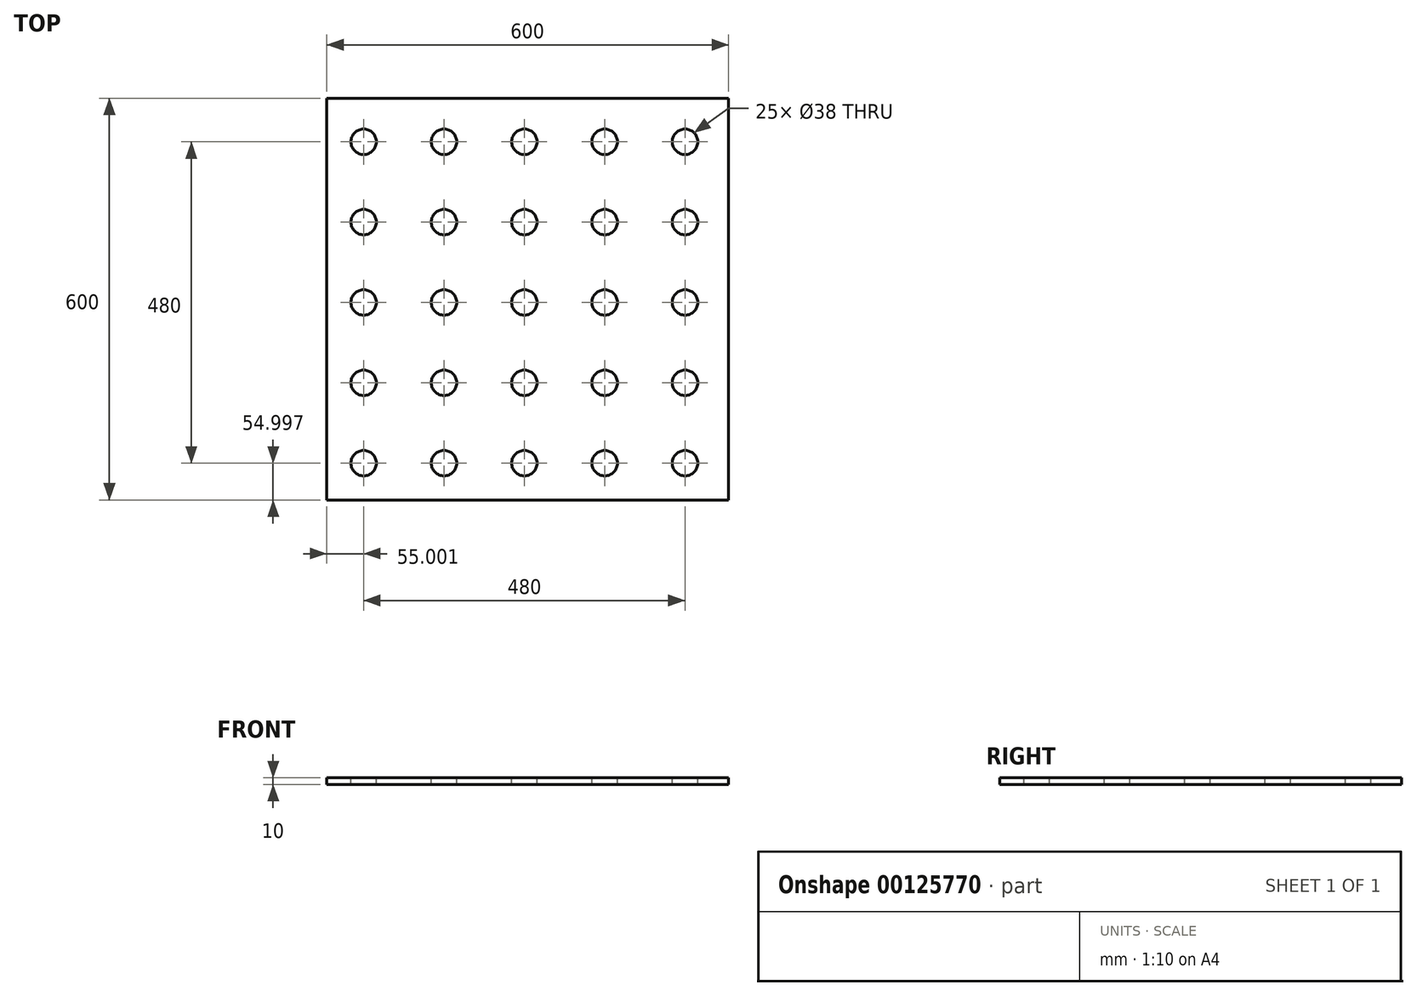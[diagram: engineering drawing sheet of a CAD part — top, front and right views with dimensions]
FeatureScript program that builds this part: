
annotation { "Feature Type Name" : "Feature", "Feature Type Description" : "" }
export const myFeature = defineFeature(function(context is Context, id is Id, definition is map)
    precondition{}
    {
        {
            var Q0;
            Q0=qCreatedBy(makeId("Top.planeOp"),FACE);
            var sketch = newSketch(context, id + "F0", { "sketchPlane" : qUnion([Q0])});
            skLineSegment(sketch, "E0.bottom", {"start": v(-275.03, 420.39) * mm, "end": v(324.97, 420.39) * mm});
            skLineSegment(sketch, "E0.top", {"start": v(-275.03, -179.61) * mm, "end": v(324.97, -179.61) * mm});
            skLineSegment(sketch, "E0.left", {"start": v(-275.03, 420.39) * mm, "end": v(-275.03, -179.61) * mm});
            skLineSegment(sketch, "E0.right", {"start": v(324.97, 420.39) * mm, "end": v(324.97, -179.61) * mm});
            skCircle(sketch, "E1", {"center": v(-220.03, -124.61) * mm, "radius": 19 * mm});
            skCircle(sketch, "E2.0.1.0", {"center": v(-220.03, -4.61) * mm, "radius": 19 * mm});
            skCircle(sketch, "E2.0.2.0", {"center": v(-220.03, 115.39) * mm, "radius": 19 * mm});
            skCircle(sketch, "E2.1.0.0", {"center": v(-100.03, -124.61) * mm, "radius": 19 * mm});
            skCircle(sketch, "E2.1.1.0", {"center": v(-100.03, -4.61) * mm, "radius": 19 * mm});
            skCircle(sketch, "E2.1.2.0", {"center": v(-100.03, 115.39) * mm, "radius": 19 * mm});
            skCircle(sketch, "E2.2.0.0", {"center": v(19.97, -124.61) * mm, "radius": 19 * mm});
            skCircle(sketch, "E2.2.1.0", {"center": v(19.97, -4.61) * mm, "radius": 19 * mm});
            skCircle(sketch, "E2.2.2.0", {"center": v(19.97, 115.39) * mm, "radius": 19 * mm});
            skLineSegment(sketch, "E2.direction1", {"start": v(-220.03, -124.61) * mm, "end": v(-100.03, -124.61) * mm, "construction": true});
            skLineSegment(sketch, "E2.direction2", {"start": v(-220.03, -124.61) * mm, "end": v(-220.03, -4.61) * mm, "construction": true});
            skCircle(sketch, "E3.0.3.0", {"center": v(139.97, -124.61) * mm, "radius": 19 * mm});
            skCircle(sketch, "E3.0.3.1", {"center": v(139.97, -4.61) * mm, "radius": 19 * mm});
            skCircle(sketch, "E3.0.3.2", {"center": v(139.97, 115.39) * mm, "radius": 19 * mm});
            skCircle(sketch, "E3.0.4.0", {"center": v(259.97, -124.61) * mm, "radius": 19 * mm});
            skCircle(sketch, "E3.0.4.1", {"center": v(259.97, -4.61) * mm, "radius": 19 * mm});
            skCircle(sketch, "E3.0.4.2", {"center": v(259.97, 115.39) * mm, "radius": 19 * mm});
            skCircle(sketch, "E4.0.0.3", {"center": v(-220.03, 235.39) * mm, "radius": 19 * mm});
            skCircle(sketch, "E4.0.1.3", {"center": v(-100.03, 235.39) * mm, "radius": 19 * mm});
            skCircle(sketch, "E4.0.2.3", {"center": v(19.97, 235.39) * mm, "radius": 19 * mm});
            skCircle(sketch, "E4.0.3.3", {"center": v(139.97, 235.39) * mm, "radius": 19 * mm});
            skCircle(sketch, "E4.0.4.3", {"center": v(259.97, 235.39) * mm, "radius": 19 * mm});
            skCircle(sketch, "E5.0.0.4", {"center": v(-220.03, 355.39) * mm, "radius": 19 * mm});
            skCircle(sketch, "E5.0.1.4", {"center": v(-100.03, 355.39) * mm, "radius": 19 * mm});
            skCircle(sketch, "E5.0.2.4", {"center": v(19.97, 355.39) * mm, "radius": 19 * mm});
            skCircle(sketch, "E5.0.3.4", {"center": v(139.97, 355.39) * mm, "radius": 19 * mm});
            skCircle(sketch, "E5.0.4.4", {"center": v(259.97, 355.39) * mm, "radius": 19 * mm});
            skSolve(sketch);
        }
        {
            var Q0;
            Q0=makeQuery(id+"F0.imprint","IMPRINT",FACE,{"disambiguationData":[TD([[makeQuery(id+"F0.imprint","IMPRINT",EDGE,{"derivedFrom":sQuery(id+"F0.wireOp",EDGE,"E0.bottom")}),-1.0]])]});
            extrude(context, id + "F1", {"entities" : qUnion([Q0]), "oppositeDirection" : true, "depth" : 10 * mm});
        }
    });
